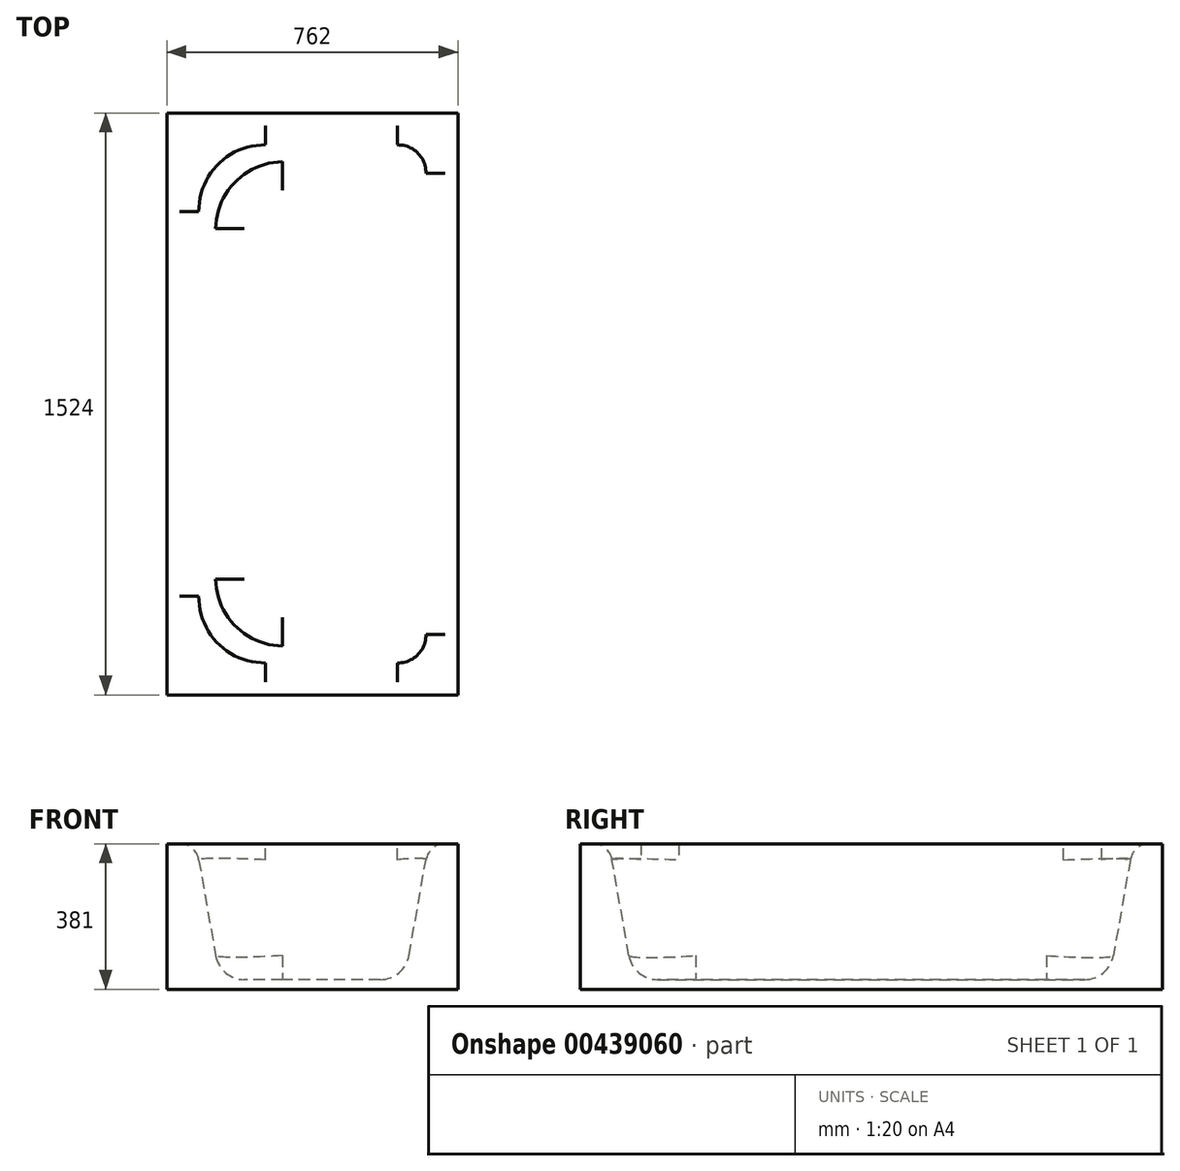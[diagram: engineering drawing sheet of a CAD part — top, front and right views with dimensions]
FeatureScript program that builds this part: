
annotation { "Feature Type Name" : "Feature", "Feature Type Description" : "" }
export const myFeature = defineFeature(function(context is Context, id is Id, definition is map)
    precondition{}
    {
        {
            var Q0;
            Q0=qCreatedBy(makeId("Top.planeOp"),FACE);
            var sketch = newSketch(context, id + "F0", { "sketchPlane" : qUnion([Q0])});
            skLineSegment(sketch, "E0.bottom", {"start": v(0, 0) * mm, "end": v(762, 0) * mm});
            skLineSegment(sketch, "E0.top", {"start": v(0, 1524) * mm, "end": v(762, 1524) * mm});
            skLineSegment(sketch, "E0.left", {"start": v(0, 0) * mm, "end": v(0, 1524) * mm});
            skLineSegment(sketch, "E0.right", {"start": v(762, 0) * mm, "end": v(762, 1524) * mm});
            skSolve(sketch);
        }
        {
            var Q0;
            Q0=qSketchRegion(id+"F0",true);
            extrude(context, id + "F1", {"entities" : qUnion([Q0]), "depth" : 381 * mm});
        }
        {
            var Q0;
            Q0=makeQuery(id+"F1.opExtrude","CAP_FACE",FACE,{"disambiguationData":[OSD([sQuery(id+"F0.wireOp",EDGE,"E0.bottom"),sQuery(id+"F0.wireOp",EDGE,"E0.top"),sQuery(id+"F0.wireOp",EDGE,"E0.left"),sQuery(id+"F0.wireOp",EDGE,"E0.right")])],"isStart":false});
            var sketch = newSketch(context, id + "F2", { "sketchPlane" : qUnion([Q0])});
            skLineSegment(sketch, "E1.bottom", {"start": v(76.2, 1447.8) * mm, "end": v(685.8, 1447.8) * mm});
            skLineSegment(sketch, "E1.top", {"start": v(76.2, 76.2) * mm, "end": v(685.8, 76.2) * mm});
            skLineSegment(sketch, "E1.left", {"start": v(76.2, 1447.8) * mm, "end": v(76.2, 76.2) * mm});
            skLineSegment(sketch, "E1.right", {"start": v(685.8, 1447.8) * mm, "end": v(685.8, 76.2) * mm});
            skSolve(sketch);
        }
        {
            var Q0;
            Q0=qSketchRegion(id+"F2",true);
            extrude(context, id + "F3", {"entities" : qUnion([Q0]), "operationType" : NewBodyOperationType.REMOVE, "oppositeDirection" : true, "depth" : 355.6 * mm, "hasDraft" : true, "draftAngle" : 10 * degree, "draftPullDirection" : true});
        }
        {
            var Q0;
            Q0=makeQuery(id+"F3.boolean.opBoolean","COPY",EDGE,{"derivedFrom":makeQuery(id+"F3.opExtrude","SWEPT_EDGE",EDGE,{"disambiguationData":[OSD([sQuery(id+"F2.wireOp",EDGE,"E1.bottom"),sQuery(id+"F2.wireOp",EDGE,"E1.left")])]})});
            var Q1;
            Q1=makeQuery(id+"F3.boolean.opBoolean","COPY",EDGE,{"derivedFrom":makeQuery(id+"F3.opExtrude","SWEPT_EDGE",EDGE,{"disambiguationData":[OSD([sQuery(id+"F2.wireOp",EDGE,"E1.top"),sQuery(id+"F2.wireOp",EDGE,"E1.left")])]})});
            fillet(context, id + "F4", {"entities" : qUnion([Q0, Q1]), "radius" : 177.8 * mm, "tangentPropagation" : true, "allowEdgeOverflow" : false});
        }
        {
            var Q0;
            Q0=makeQuery(id+"F3.boolean.opBoolean","COPY",EDGE,{"derivedFrom":makeQuery(id+"F3.opExtrude","SWEPT_EDGE",EDGE,{"disambiguationData":[OSD([sQuery(id+"F2.wireOp",EDGE,"E1.bottom"),sQuery(id+"F2.wireOp",EDGE,"E1.right")])]})});
            var Q1;
            Q1=makeQuery(id+"F3.boolean.opBoolean","COPY",EDGE,{"derivedFrom":makeQuery(id+"F3.opExtrude","SWEPT_EDGE",EDGE,{"disambiguationData":[OSD([sQuery(id+"F2.wireOp",EDGE,"E1.top"),sQuery(id+"F2.wireOp",EDGE,"E1.right")])]})});
            fillet(context, id + "F5", {"entities" : qUnion([Q0, Q1]), "radius" : 76.2 * mm, "tangentPropagation" : true, "allowEdgeOverflow" : false});
        }
        {
            var Q0;
            {var subQ0=sQuery(id+"F2.wireOp",EDGE,"E1.left");var subQ1=sQuery(id+"F2.wireOp",EDGE,"E1.bottom");Q0=makeQuery(id+"F4.opFillet","BLEND_EDGE",EDGE,{"blendedFrom":[makeQuery(id+"F3.boolean.opBoolean","COPY",EDGE,{"derivedFrom":makeQuery(id+"F3.opExtrude","SWEPT_EDGE",EDGE,{"disambiguationData":[OSD([subQ1,subQ0])]})}),makeQuery(id+"F3.boolean.opBoolean","COPY",FACE,{"derivedFrom":makeQuery(id+"F3.opExtrude","CAP_FACE",FACE,{"disambiguationData":[OSD([subQ1,sQuery(id+"F2.wireOp",EDGE,"E1.top"),subQ0,sQuery(id+"F2.wireOp",EDGE,"E1.right")])],"isStart":false})})],"blendedInto":[makeQuery(id+"F3.boolean.opBoolean","COPY",FACE,{"derivedFrom":makeQuery(id+"F3.opExtrude","CAP_FACE",FACE,{"disambiguationData":[OSD([subQ1,sQuery(id+"F2.wireOp",EDGE,"E1.top"),subQ0,sQuery(id+"F2.wireOp",EDGE,"E1.right")])],"isStart":false})})]});}
            var Q1;
            Q1=makeQuery(id+"F3.boolean.opBoolean","COPY",EDGE,{"derivedFrom":makeQuery(id+"F3.opExtrude","CAP_EDGE",EDGE,{"disambiguationData":[OSD([sQuery(id+"F2.wireOp",EDGE,"E1.bottom")])],"isStart":false})});
            var Q2;
            {var subQ0=sQuery(id+"F2.wireOp",EDGE,"E1.right");var subQ1=sQuery(id+"F2.wireOp",EDGE,"E1.bottom");Q2=makeQuery(id+"F5.opFillet","BLEND_EDGE",EDGE,{"blendedFrom":[makeQuery(id+"F3.boolean.opBoolean","COPY",EDGE,{"derivedFrom":makeQuery(id+"F3.opExtrude","SWEPT_EDGE",EDGE,{"disambiguationData":[OSD([subQ1,subQ0])]})}),makeQuery(id+"F3.boolean.opBoolean","COPY",FACE,{"derivedFrom":makeQuery(id+"F3.opExtrude","CAP_FACE",FACE,{"disambiguationData":[OSD([subQ1,sQuery(id+"F2.wireOp",EDGE,"E1.top"),sQuery(id+"F2.wireOp",EDGE,"E1.left"),subQ0])],"isStart":false})})],"blendedInto":[makeQuery(id+"F3.boolean.opBoolean","COPY",FACE,{"derivedFrom":makeQuery(id+"F3.opExtrude","CAP_FACE",FACE,{"disambiguationData":[OSD([subQ1,sQuery(id+"F2.wireOp",EDGE,"E1.top"),sQuery(id+"F2.wireOp",EDGE,"E1.left"),subQ0])],"isStart":false})})]});}
            var Q3;
            {var subQ0=sQuery(id+"F2.wireOp",EDGE,"E1.right");var subQ1=sQuery(id+"F2.wireOp",EDGE,"E1.top");Q3=makeQuery(id+"F5.opFillet","BLEND_EDGE",EDGE,{"blendedFrom":[makeQuery(id+"F3.boolean.opBoolean","COPY",EDGE,{"derivedFrom":makeQuery(id+"F3.opExtrude","SWEPT_EDGE",EDGE,{"disambiguationData":[OSD([subQ1,subQ0])]})}),makeQuery(id+"F3.boolean.opBoolean","COPY",FACE,{"derivedFrom":makeQuery(id+"F3.opExtrude","CAP_FACE",FACE,{"disambiguationData":[OSD([sQuery(id+"F2.wireOp",EDGE,"E1.bottom"),subQ1,sQuery(id+"F2.wireOp",EDGE,"E1.left"),subQ0])],"isStart":false})})],"blendedInto":[makeQuery(id+"F3.boolean.opBoolean","COPY",FACE,{"derivedFrom":makeQuery(id+"F3.opExtrude","CAP_FACE",FACE,{"disambiguationData":[OSD([sQuery(id+"F2.wireOp",EDGE,"E1.bottom"),subQ1,sQuery(id+"F2.wireOp",EDGE,"E1.left"),subQ0])],"isStart":false})})]});}
            var Q4;
            Q4=makeQuery(id+"F3.boolean.opBoolean","COPY",EDGE,{"derivedFrom":makeQuery(id+"F3.opExtrude","CAP_EDGE",EDGE,{"disambiguationData":[OSD([sQuery(id+"F2.wireOp",EDGE,"E1.top")])],"isStart":false})});
            var Q5;
            {var subQ0=sQuery(id+"F2.wireOp",EDGE,"E1.left");var subQ1=sQuery(id+"F2.wireOp",EDGE,"E1.top");Q5=makeQuery(id+"F4.opFillet","BLEND_EDGE",EDGE,{"blendedFrom":[makeQuery(id+"F3.boolean.opBoolean","COPY",EDGE,{"derivedFrom":makeQuery(id+"F3.opExtrude","SWEPT_EDGE",EDGE,{"disambiguationData":[OSD([subQ1,subQ0])]})}),makeQuery(id+"F3.boolean.opBoolean","COPY",FACE,{"derivedFrom":makeQuery(id+"F3.opExtrude","CAP_FACE",FACE,{"disambiguationData":[OSD([sQuery(id+"F2.wireOp",EDGE,"E1.bottom"),subQ1,subQ0,sQuery(id+"F2.wireOp",EDGE,"E1.right")])],"isStart":false})})],"blendedInto":[makeQuery(id+"F3.boolean.opBoolean","COPY",FACE,{"derivedFrom":makeQuery(id+"F3.opExtrude","CAP_FACE",FACE,{"disambiguationData":[OSD([sQuery(id+"F2.wireOp",EDGE,"E1.bottom"),subQ1,subQ0,sQuery(id+"F2.wireOp",EDGE,"E1.right")])],"isStart":false})})]});}
            var Q6;
            Q6=makeQuery(id+"F3.boolean.opBoolean","COPY",EDGE,{"derivedFrom":makeQuery(id+"F3.opExtrude","CAP_EDGE",EDGE,{"disambiguationData":[OSD([sQuery(id+"F2.wireOp",EDGE,"E1.left")])],"isStart":false})});
            var Q7;
            Q7=makeQuery(id+"F3.boolean.opBoolean","COPY",EDGE,{"derivedFrom":makeQuery(id+"F3.opExtrude","CAP_EDGE",EDGE,{"disambiguationData":[OSD([sQuery(id+"F2.wireOp",EDGE,"E1.right")])],"isStart":false})});
            fillet(context, id + "F6", {"entities" : qUnion([Q0, Q1, Q2, Q3, Q4, Q5, Q6, Q7]), "radius" : 76.2 * mm, "tangentPropagation" : true, "allowEdgeOverflow" : false});
        }
        {
            var Q0;
            Q0=makeQuery(id+"F4.opFillet","BLEND_EDGE",EDGE,{"blendedFrom":[makeQuery(id+"F3.boolean.opBoolean","COPY",EDGE,{"derivedFrom":makeQuery(id+"F3.opExtrude","SWEPT_EDGE",EDGE,{"disambiguationData":[OSD([sQuery(id+"F2.wireOp",EDGE,"E1.bottom"),sQuery(id+"F2.wireOp",EDGE,"E1.left")])]})}),makeQuery(id+"F1.opExtrude","CAP_FACE",FACE,{"disambiguationData":[OSD([sQuery(id+"F0.wireOp",EDGE,"E0.bottom"),sQuery(id+"F0.wireOp",EDGE,"E0.top"),sQuery(id+"F0.wireOp",EDGE,"E0.left"),sQuery(id+"F0.wireOp",EDGE,"E0.right")])],"isStart":false})],"blendedInto":[makeQuery(id+"F1.opExtrude","CAP_FACE",FACE,{"disambiguationData":[OSD([sQuery(id+"F0.wireOp",EDGE,"E0.bottom"),sQuery(id+"F0.wireOp",EDGE,"E0.top"),sQuery(id+"F0.wireOp",EDGE,"E0.left"),sQuery(id+"F0.wireOp",EDGE,"E0.right")])],"isStart":false})]});
            var Q1;
            Q1=makeQuery(id+"F3.boolean.opBoolean","COPY",EDGE,{"derivedFrom":makeQuery(id+"F3.opExtrude","CAP_EDGE",EDGE,{"disambiguationData":[OSD([sQuery(id+"F2.wireOp",EDGE,"E1.left")])],"isStart":true})});
            var Q2;
            Q2=makeQuery(id+"F4.opFillet","BLEND_EDGE",EDGE,{"blendedFrom":[makeQuery(id+"F3.boolean.opBoolean","COPY",EDGE,{"derivedFrom":makeQuery(id+"F3.opExtrude","SWEPT_EDGE",EDGE,{"disambiguationData":[OSD([sQuery(id+"F2.wireOp",EDGE,"E1.top"),sQuery(id+"F2.wireOp",EDGE,"E1.left")])]})}),makeQuery(id+"F1.opExtrude","CAP_FACE",FACE,{"disambiguationData":[OSD([sQuery(id+"F0.wireOp",EDGE,"E0.bottom"),sQuery(id+"F0.wireOp",EDGE,"E0.top"),sQuery(id+"F0.wireOp",EDGE,"E0.left"),sQuery(id+"F0.wireOp",EDGE,"E0.right")])],"isStart":false})],"blendedInto":[makeQuery(id+"F1.opExtrude","CAP_FACE",FACE,{"disambiguationData":[OSD([sQuery(id+"F0.wireOp",EDGE,"E0.bottom"),sQuery(id+"F0.wireOp",EDGE,"E0.top"),sQuery(id+"F0.wireOp",EDGE,"E0.left"),sQuery(id+"F0.wireOp",EDGE,"E0.right")])],"isStart":false})]});
            var Q3;
            Q3=makeQuery(id+"F3.boolean.opBoolean","COPY",EDGE,{"derivedFrom":makeQuery(id+"F3.opExtrude","CAP_EDGE",EDGE,{"disambiguationData":[OSD([sQuery(id+"F2.wireOp",EDGE,"E1.top")])],"isStart":true})});
            var Q4;
            Q4=makeQuery(id+"F5.opFillet","BLEND_EDGE",EDGE,{"blendedFrom":[makeQuery(id+"F3.boolean.opBoolean","COPY",EDGE,{"derivedFrom":makeQuery(id+"F3.opExtrude","SWEPT_EDGE",EDGE,{"disambiguationData":[OSD([sQuery(id+"F2.wireOp",EDGE,"E1.top"),sQuery(id+"F2.wireOp",EDGE,"E1.right")])]})}),makeQuery(id+"F1.opExtrude","CAP_FACE",FACE,{"disambiguationData":[OSD([sQuery(id+"F0.wireOp",EDGE,"E0.bottom"),sQuery(id+"F0.wireOp",EDGE,"E0.top"),sQuery(id+"F0.wireOp",EDGE,"E0.left"),sQuery(id+"F0.wireOp",EDGE,"E0.right")])],"isStart":false})],"blendedInto":[makeQuery(id+"F1.opExtrude","CAP_FACE",FACE,{"disambiguationData":[OSD([sQuery(id+"F0.wireOp",EDGE,"E0.bottom"),sQuery(id+"F0.wireOp",EDGE,"E0.top"),sQuery(id+"F0.wireOp",EDGE,"E0.left"),sQuery(id+"F0.wireOp",EDGE,"E0.right")])],"isStart":false})]});
            var Q5;
            Q5=makeQuery(id+"F3.boolean.opBoolean","COPY",EDGE,{"derivedFrom":makeQuery(id+"F3.opExtrude","CAP_EDGE",EDGE,{"disambiguationData":[OSD([sQuery(id+"F2.wireOp",EDGE,"E1.right")])],"isStart":true})});
            var Q6;
            Q6=makeQuery(id+"F5.opFillet","BLEND_EDGE",EDGE,{"blendedFrom":[makeQuery(id+"F3.boolean.opBoolean","COPY",EDGE,{"derivedFrom":makeQuery(id+"F3.opExtrude","SWEPT_EDGE",EDGE,{"disambiguationData":[OSD([sQuery(id+"F2.wireOp",EDGE,"E1.bottom"),sQuery(id+"F2.wireOp",EDGE,"E1.right")])]})}),makeQuery(id+"F1.opExtrude","CAP_FACE",FACE,{"disambiguationData":[OSD([sQuery(id+"F0.wireOp",EDGE,"E0.bottom"),sQuery(id+"F0.wireOp",EDGE,"E0.top"),sQuery(id+"F0.wireOp",EDGE,"E0.left"),sQuery(id+"F0.wireOp",EDGE,"E0.right")])],"isStart":false})],"blendedInto":[makeQuery(id+"F1.opExtrude","CAP_FACE",FACE,{"disambiguationData":[OSD([sQuery(id+"F0.wireOp",EDGE,"E0.bottom"),sQuery(id+"F0.wireOp",EDGE,"E0.top"),sQuery(id+"F0.wireOp",EDGE,"E0.left"),sQuery(id+"F0.wireOp",EDGE,"E0.right")])],"isStart":false})]});
            var Q7;
            Q7=makeQuery(id+"F3.boolean.opBoolean","COPY",EDGE,{"derivedFrom":makeQuery(id+"F3.opExtrude","CAP_EDGE",EDGE,{"disambiguationData":[OSD([sQuery(id+"F2.wireOp",EDGE,"E1.bottom")])],"isStart":true})});
            fillet(context, id + "F7", {"entities" : qUnion([Q0, Q1, Q2, Q3, Q4, Q5, Q6, Q7]), "radius" : 50.8 * mm, "tangentPropagation" : true, "allowEdgeOverflow" : false});
        }
    });
